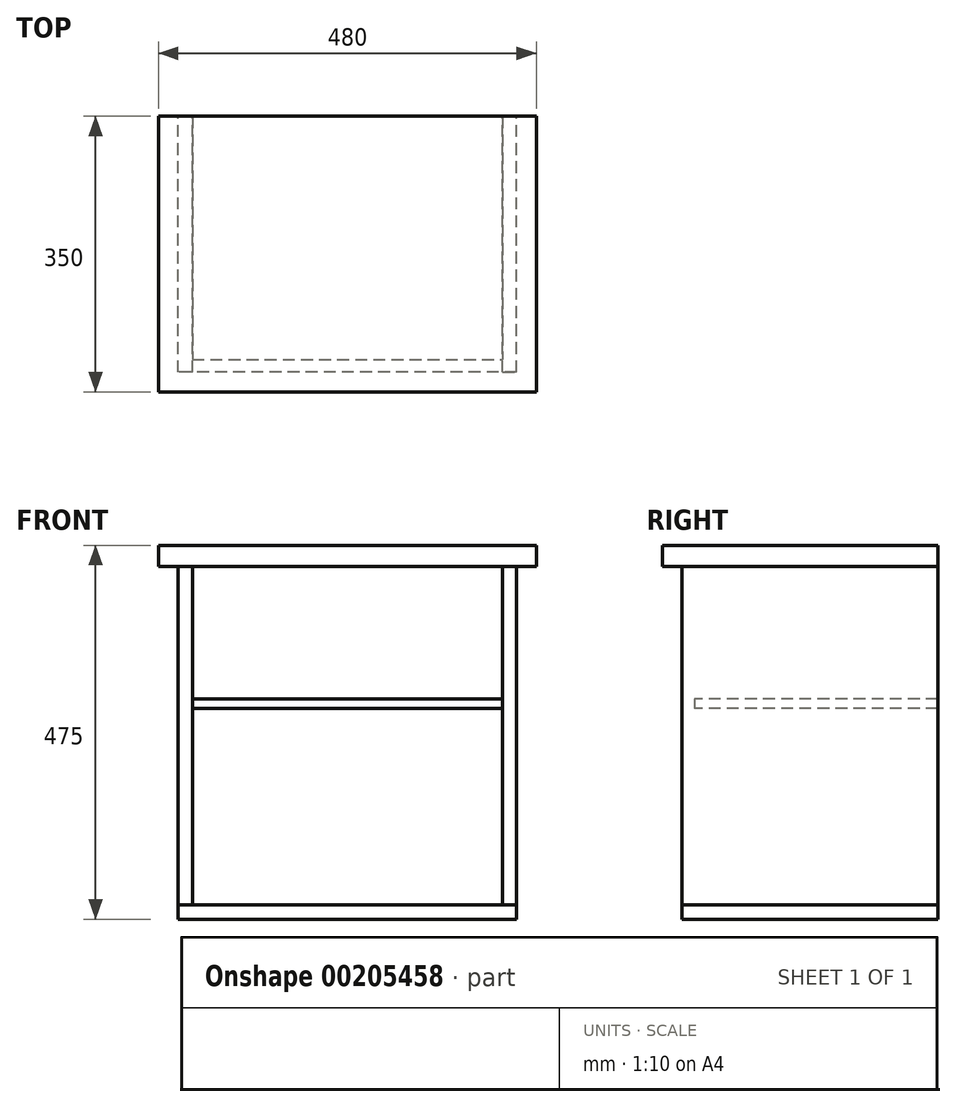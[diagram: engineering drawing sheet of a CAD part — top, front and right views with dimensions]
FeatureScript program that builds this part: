
annotation { "Feature Type Name" : "Feature", "Feature Type Description" : "" }
export const myFeature = defineFeature(function(context is Context, id is Id, definition is map)
    precondition{}
    {
        {
            var Q0;
            Q0=qCreatedBy(makeId("Top.planeOp"),FACE);
            var sketch = newSketch(context, id + "F0", { "sketchPlane" : qUnion([Q0])});
            skLineSegment(sketch, "E0.bottom", {"start": v(215, -162.5) * mm, "end": v(-215, -162.5) * mm});
            skLineSegment(sketch, "E0.top", {"start": v(215, 162.5) * mm, "end": v(-215, 162.5) * mm});
            skLineSegment(sketch, "E0.left", {"start": v(215, -162.5) * mm, "end": v(215, 162.5) * mm});
            skLineSegment(sketch, "E0.right", {"start": v(-215, -162.5) * mm, "end": v(-215, 162.5) * mm});
            skPoint(sketch, "E0.middle", {"position": v(0, 0) * mm});
            skSolve(sketch);
        }
        {
            var Q0;
            Q0=makeQuery(id+"F0.imprint","IMPRINT",FACE,{"disambiguationData":[TD([[makeQuery(id+"F0.imprint","IMPRINT",EDGE,{"derivedFrom":sQuery(id+"F0.wireOp",EDGE,"E0.bottom")}),-1.0]])]});
            extrude(context, id + "F1", {"entities" : qUnion([Q0]), "depth" : 18 * mm});
        }
        {
            var Q0;
            Q0=makeQuery(id+"F1.opExtrude","SWEPT_FACE",FACE,{"disambiguationData":[OSD([sQuery(id+"F0.wireOp",EDGE,"E0.left")])]});
            var sketch = newSketch(context, id + "F2", { "sketchPlane" : qUnion([Q0])});
            skLineSegment(sketch, "E1.bottom", {"start": v(-162.5, 18) * mm, "end": v(162.5, 18) * mm});
            skLineSegment(sketch, "E1.top", {"start": v(-162.5, 448) * mm, "end": v(162.5, 448) * mm});
            skLineSegment(sketch, "E1.left", {"start": v(-162.5, 18) * mm, "end": v(-162.5, 448) * mm});
            skLineSegment(sketch, "E1.right", {"start": v(162.5, 18) * mm, "end": v(162.5, 448) * mm});
            skSolve(sketch);
        }
        {
            var Q0;
            Q0=makeQuery(id+"F2.imprint","IMPRINT",FACE,{"disambiguationData":[TD([[makeQuery(id+"F2.imprint","IMPRINT",EDGE,{"derivedFrom":sQuery(id+"F2.wireOp",EDGE,"E1.bottom")}),1.0]])]});
            extrude(context, id + "F3", {"entities" : qUnion([Q0]), "oppositeDirection" : true, "depth" : 18 * mm});
        }
        {
            var Q0;
            Q0=makeQuery(id+"F3.opExtrude","SWEPT_BODY",BODY,{"disambiguationData":[OSD([sQuery(id+"F2.wireOp",EDGE,"E1.bottom"),sQuery(id+"F2.wireOp",EDGE,"E1.top"),sQuery(id+"F2.wireOp",EDGE,"E1.left"),sQuery(id+"F2.wireOp",EDGE,"E1.right")])]});
            var Q1;
            Q1=qCreatedBy(makeId("Right.planeOp"),FACE);
            mirror(context, id + "F4", {"entities" : qUnion([Q0]), "mirrorPlane" : qUnion([Q1])});
        }
        {
            var Q0;
            Q0=makeQuery(id+"F3.opExtrude","SWEPT_FACE",FACE,{"disambiguationData":[OSD([sQuery(id+"F2.wireOp",EDGE,"E1.top")])]});
            var sketch = newSketch(context, id + "F5", { "sketchPlane" : qUnion([Q0])});
            skLineSegment(sketch, "E2.bottom", {"start": v(-240, 162.5) * mm, "end": v(240, 162.5) * mm});
            skLineSegment(sketch, "E2.top", {"start": v(-240, -187.5) * mm, "end": v(240, -187.5) * mm});
            skLineSegment(sketch, "E2.left", {"start": v(-240, 162.5) * mm, "end": v(-240, -187.5) * mm});
            skLineSegment(sketch, "E2.right", {"start": v(240, 162.5) * mm, "end": v(240, -187.5) * mm});
            skSolve(sketch);
        }
        {
            var Q0;
            Q0 = qSketchRegion(id + "F5", true);
            extrude(context, id + "F6", {"entities" : qUnion([Q0]), "depth" : 27 * mm});
        }
        {
            var Q0;
            Q0=makeQuery(id+"F1.opExtrude","CAP_FACE",FACE,{"disambiguationData":[OSD([sQuery(id+"F0.wireOp",EDGE,"E0.bottom"),sQuery(id+"F0.wireOp",EDGE,"E0.top"),sQuery(id+"F0.wireOp",EDGE,"E0.left"),sQuery(id+"F0.wireOp",EDGE,"E0.right")])],"isStart":false});
            cPlane(context, id + "F7", {"entities" : qUnion([Q0]), "cplaneType" : CPlaneType.OFFSET, "offset" : 250 * mm, "width" : 150 * mm, "height" : 150 * mm});
        }
        {
            var Q0;
            Q0=qCreatedBy(id+"F7.planeOp",FACE);
            var sketch = newSketch(context, id + "F8", { "sketchPlane" : qUnion([Q0])});
            skLineSegment(sketch, "E3.bottom", {"start": v(-197, 162.5) * mm, "end": v(197, 162.5) * mm});
            skLineSegment(sketch, "E3.top", {"start": v(-197, -146.5) * mm, "end": v(197, -146.5) * mm});
            skLineSegment(sketch, "E3.left", {"start": v(-197, 162.5) * mm, "end": v(-197, -146.5) * mm});
            skLineSegment(sketch, "E3.right", {"start": v(197, 162.5) * mm, "end": v(197, -146.5) * mm});
            skSolve(sketch);
        }
        {
            var Q0;
            Q0 = qSketchRegion(id + "F8", true);
            extrude(context, id + "F9", {"entities" : qUnion([Q0]), "depth" : 12 * mm});
        }
    });
